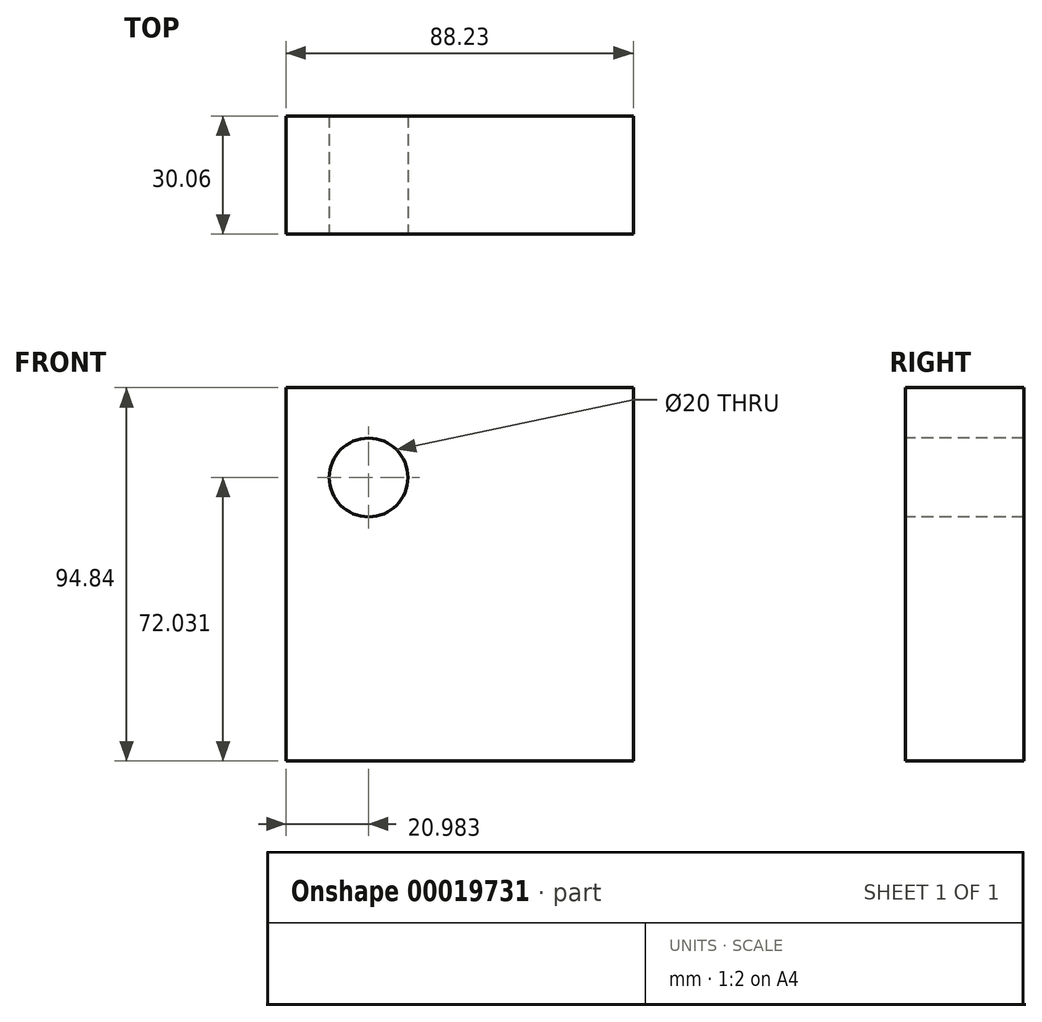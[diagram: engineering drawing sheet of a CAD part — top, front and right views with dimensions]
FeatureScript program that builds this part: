
annotation { "Feature Type Name" : "Feature", "Feature Type Description" : "" }
export const myFeature = defineFeature(function(context is Context, id is Id, definition is map)
    precondition{}
    {
        {
            var Q0;
            Q0=qCreatedBy(makeId("Front.planeOp"),FACE);
            var sketch = newSketch(context, id + "F0", { "sketchPlane" : qUnion([Q0])});
            skLineSegment(sketch, "E0.bottom", {"start": v(-62.83, 53.49) * mm, "end": v(25.4, 53.49) * mm});
            skLineSegment(sketch, "E0.top", {"start": v(-62.83, -41.35) * mm, "end": v(25.4, -41.35) * mm});
            skLineSegment(sketch, "E0.left", {"start": v(-62.83, 53.49) * mm, "end": v(-62.83, -41.35) * mm});
            skLineSegment(sketch, "E1", {"start": v(25.4, 53.49) * mm, "end": v(25.4, -41.35) * mm});
            skSolve(sketch);
        }
        {
            var Q0;
            Q0=makeQuery(id+"F0.imprint","IMPRINT",FACE,{"disambiguationData":[TD([[makeQuery(id+"F0.imprint","IMPRINT",EDGE,{"derivedFrom":sQuery(id+"F0.wireOp",EDGE,"E0.bottom")}),-1.0]])]});
            extrude(context, id + "F1", {"entities" : qUnion([Q0]), "depth" : 30.06 * mm});
        }
        {
            var Q0;
            Q0=makeQuery(id+"F1.opExtrude","CAP_FACE",FACE,{"disambiguationData":[OSD([sQuery(id+"F0.wireOp",EDGE,"E0.bottom"),sQuery(id+"F0.wireOp",EDGE,"E0.top"),sQuery(id+"F0.wireOp",EDGE,"E0.left"),sQuery(id+"F0.wireOp",EDGE,"E1")])],"isStart":false});
            var sketch = newSketch(context, id + "F2", { "sketchPlane" : qUnion([Q0])});
            skCircle(sketch, "E2", {"center": v(-41.85, 30.68) * mm, "radius": 10 * mm});
            skSolve(sketch);
        }
        {
            var Q0;
            Q0=makeQuery(id+"F2.imprint","IMPRINT",FACE,{"disambiguationData":[TD([[makeQuery(id+"F2.imprint","IMPRINT",EDGE,{"derivedFrom":sQuery(id+"F2.wireOp",EDGE,"E2")}),1.0]])]});
            extrude(context, id + "F3", {"entities" : qUnion([Q0]), "operationType" : NewBodyOperationType.REMOVE, "endBound" : BoundingType.THROUGH_ALL, "oppositeDirection" : true, "depth" : 25 * mm});
        }
        {
            var Q0;
            Q0=sQuery(id+"F2.wireOp",EDGE,"E2");
            extrude(context, id + "F4", {"bodyType" : ToolBodyType.SURFACE, "surfaceEntities" : qUnion([Q0]), "endBound" : BoundingType.THROUGH_ALL, "oppositeDirection" : true, "depth" : 25 * mm});
        }
    });
